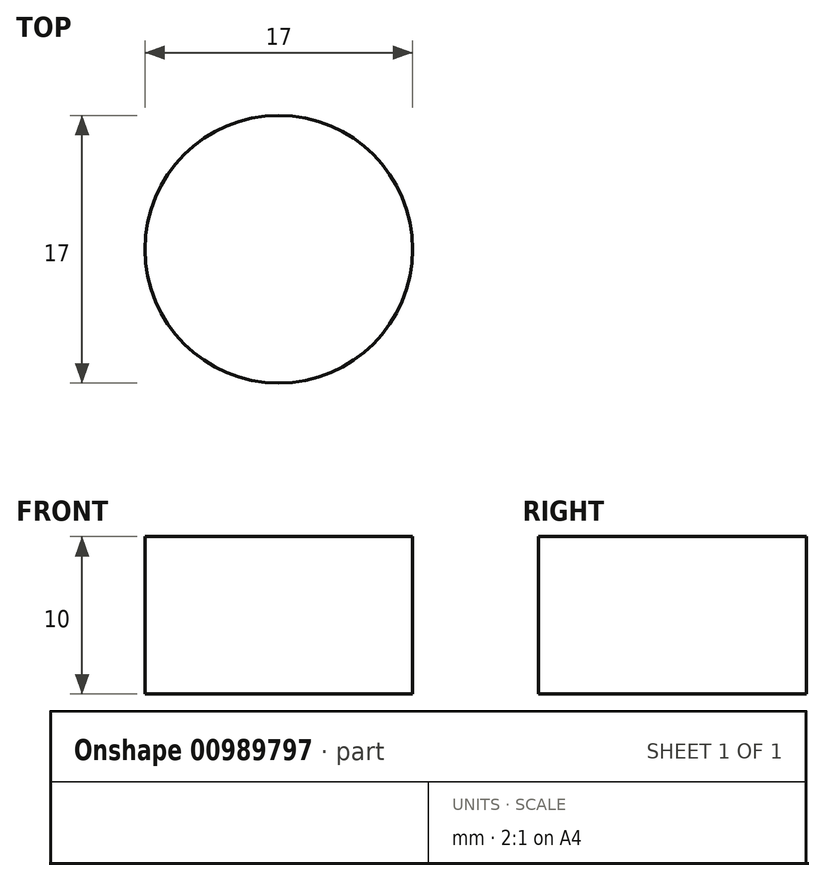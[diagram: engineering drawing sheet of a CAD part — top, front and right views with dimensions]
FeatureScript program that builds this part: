
annotation { "Feature Type Name" : "Feature", "Feature Type Description" : "" }
export const myFeature = defineFeature(function(context is Context, id is Id, definition is map)
    precondition{}
    {
        {
            var Q0;
            Q0=qCreatedBy(makeId("Top.planeOp"),FACE);
            var sketch = newSketch(context, id + "F0", { "sketchPlane" : qUnion([Q0])});
            skCircle(sketch, "E0", {"center": v(0, 0) * mm, "radius": 8.5 * mm});
            skSolve(sketch);
        }
        {
            var Q0;
            Q0 = qSketchRegion(id + "F0", true);
            extrude(context, id + "F1", {"entities" : qUnion([Q0]), "depth" : 10 * mm, "offsetDistance" : 25 * mm});
        }
    });
